# Revit family: CONV_Flokk_OffcChrs_RBMNoor6055
name_source: partatom
category: Furniture
revit_build: Autodesk Revit 2015 (Build: 20140606_1530(x64)
units: mm (PartAtom-declared; Revit-internal decimal feet)

## types (1)
- CONV_Flokk_OffcChrs_RBMNoor6055
    AssetType = Movable
    BIMObjectName = CONV_Flokk_OffcChrs_RBMNoor6055
    Brand = RBM
    Category = Meeting chair
    Collection = RBM Noor
    Color = Various
    ConvergoRefNr = 0119-1802-0042-NO
    Cost = 0 $
    Designer = StokkeAustad, Form Us With Love, Susanne Gronlund, Scandinavian Business Seating
    DurationUnit = Year
    ExpiringDate = 08/2018
    Features = Armrests, modular structure
armrests (optional extra), armrest height, armrest width,
seat height, seat depth, lumbar support, tilt resistance/HÅG
inBalance™, lockable tilt and foot support
    HighestSeatingHeight = 437 mm  [stored 1.43373 ft]
    IfcExportAs = IfcFurnishingElementType
    IfcExportType = CHAIR
    LowestSeatingHeight = 437 mm  [stored 1.43373 ft]
    MainColor = Various
    Manufacturer = Flokk
    ManufacturerName = Flokk
    ManufacturerURL = https://www.flokk.com
    Material = Wood, metal
    Model = RBM Noor 6055
    ModelNumber = 6055
    NBSDescription = Stacking chairs
    NBSReference = 45-35-20/355
    Name = OffcChrs_RBMNoor6055
    NominalDepth = 530 mm  [stored 1.73885 ft]
    NominalHeight = 831 mm  [stored 2.72638 ft]
    NominalLength = 543 mm  [stored 1.7815 ft]
    OfficeChairTertiaryMaterial = Plastic, Opaque Black
    ProductInformation = RBM Noor 4-leg is lean and lightweight. The RBM Noor 6055 comes with a 3D veneer shell in natural or dark-stained oak which you can mix-and-match with various tubular steel leg colours. Armrests are optional. The chair is an easy-to-stack chair that’s perfectly apt for most dining areas, meeting rooms or study environments, along with your home.
    SeatingHeight = 437 mm  [stored 1.43373 ft]
    Shape = Sculptured
    Size = 543x543x830 mm
    URL = https://www.flokk.com
    Uniclass2 = Pr_40_50_12_51
    Uniclass2015Description = Meeting room chairs
    Uniclass2015Reference = Pr_40_50_12_51
    Version = 1
    VersionDate = 12/03/2018
    WarrantyDurationUnit = Year
    Weight = 4.8 kg

note: [stored X ft] marks values corroborated as IEEE doubles in the binary element streams (Revit-internal decimal feet)

## geometry (parser evidence)
native form markers: Blend x8, Sweep x12
no freeform markers — native parametric forms only
